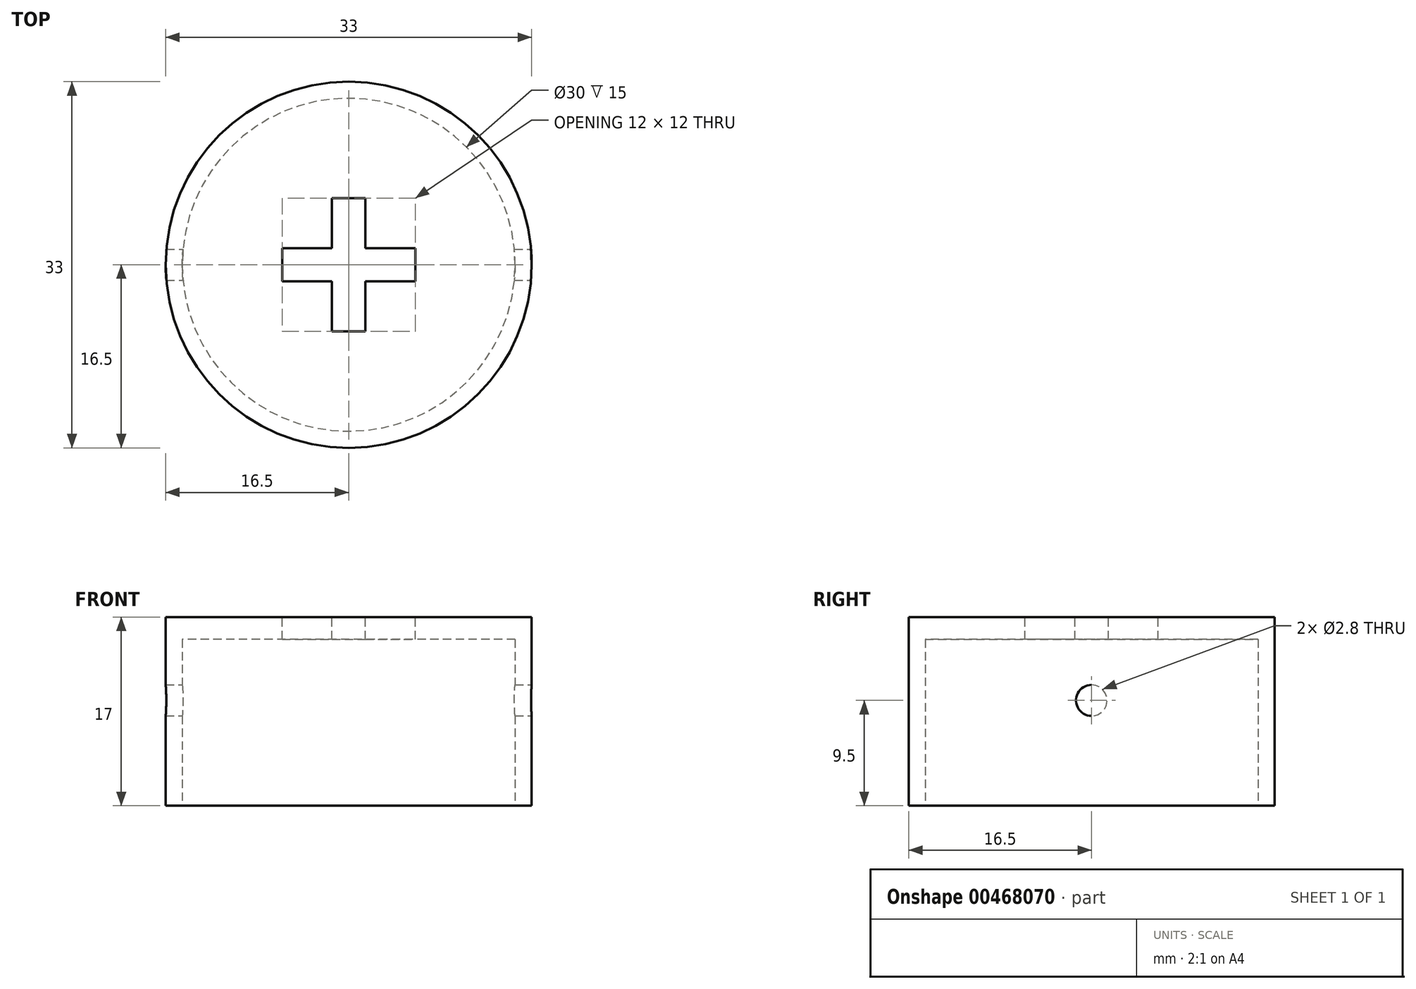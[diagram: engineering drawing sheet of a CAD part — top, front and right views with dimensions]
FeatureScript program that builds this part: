
annotation { "Feature Type Name" : "Feature", "Feature Type Description" : "" }
export const myFeature = defineFeature(function(context is Context, id is Id, definition is map)
    precondition{}
    {
        {
            var Q0;
            Q0=qCreatedBy(makeId("Top.planeOp"),FACE);
            var sketch = newSketch(context, id + "F0", { "sketchPlane" : qUnion([Q0])});
            skCircle(sketch, "E0", {"center": v(0, 0) * mm, "radius": 16.5 * mm});
            skSolve(sketch);
        }
        {
            var Q0;
            Q0=makeQuery(id+"F0.imprint","IMPRINT",FACE,{"disambiguationData":[TD([[makeQuery(id+"F0.imprint","IMPRINT",EDGE,{"derivedFrom":sQuery(id+"F0.wireOp",EDGE,"E0")}),1.0]])]});
            extrude(context, id + "F1", {"entities" : qUnion([Q0]), "depth" : 17 * mm});
        }
        {
            var Q0;
            Q0=qCreatedBy(makeId("Top.planeOp"),FACE);
            var sketch = newSketch(context, id + "F2", { "sketchPlane" : qUnion([Q0])});
            skCircle(sketch, "E1", {"center": v(0, 0) * mm, "radius": 15 * mm});
            skSolve(sketch);
        }
        {
            var Q0;
            Q0 = qSketchRegion(id + "F2", true);
            extrude(context, id + "F3", {"entities" : qUnion([Q0]), "operationType" : NewBodyOperationType.REMOVE, "depth" : 15 * mm});
        }
        {
            var Q0;
            Q0=qCreatedBy(makeId("Right.planeOp"),FACE);
            var sketch = newSketch(context, id + "F4", { "sketchPlane" : qUnion([Q0])});
            skCircle(sketch, "E2", {"center": v(0, 9.5) * mm, "radius": 1.4 * mm});
            skSolve(sketch);
        }
        {
            var Q0;
            Q0 = qSketchRegion(id + "F4", true);
            extrude(context, id + "F5", {"entities" : qUnion([Q0]), "operationType" : NewBodyOperationType.REMOVE, "endBound" : BoundingType.SYMMETRIC, "oppositeDirection" : true, "depth" : 40 * mm});
        }
        {
            var Q0;
            Q0=makeQuery(id+"F1.opExtrude","CAP_FACE",FACE,{"disambiguationData":[OSD([sQuery(id+"F0.wireOp",EDGE,"E0")])],"isStart":false});
            var sketch = newSketch(context, id + "F6", { "sketchPlane" : qUnion([Q0])});
            skLineSegment(sketch, "E3.bottom", {"start": v(-1.5, 6) * mm, "end": v(1.5, 6) * mm});
            skLineSegment(sketch, "E3.top", {"start": v(-1.5, -6) * mm, "end": v(1.5, -6) * mm});
            skLineSegment(sketch, "E3.left", {"start": v(-1.5, 6) * mm, "end": v(-1.5, -6) * mm});
            skLineSegment(sketch, "E3.right", {"start": v(1.5, 6) * mm, "end": v(1.5, -6) * mm});
            skLineSegment(sketch, "E4.bottom", {"start": v(-6, 1.5) * mm, "end": v(6, 1.5) * mm});
            skLineSegment(sketch, "E4.top", {"start": v(-6, -1.5) * mm, "end": v(6, -1.5) * mm});
            skLineSegment(sketch, "E4.left", {"start": v(-6, 1.5) * mm, "end": v(-6, -1.5) * mm});
            skLineSegment(sketch, "E4.right", {"start": v(6, 1.5) * mm, "end": v(6, -1.5) * mm});
            skLineSegment(sketch, "E5", {"start": v(1.5, 6) * mm, "end": v(-1.5, -6) * mm});
            skLineSegment(sketch, "E6", {"start": v(-6, -1.5) * mm, "end": v(6, 1.5) * mm});
            skSolve(sketch);
        }
        {
            var Q0;
            Q0 = qSketchRegion(id + "F6", true);
            extrude(context, id + "F7", {"entities" : qUnion([Q0]), "operationType" : NewBodyOperationType.REMOVE, "oppositeDirection" : true, "depth" : 2 * mm});
        }
    });
